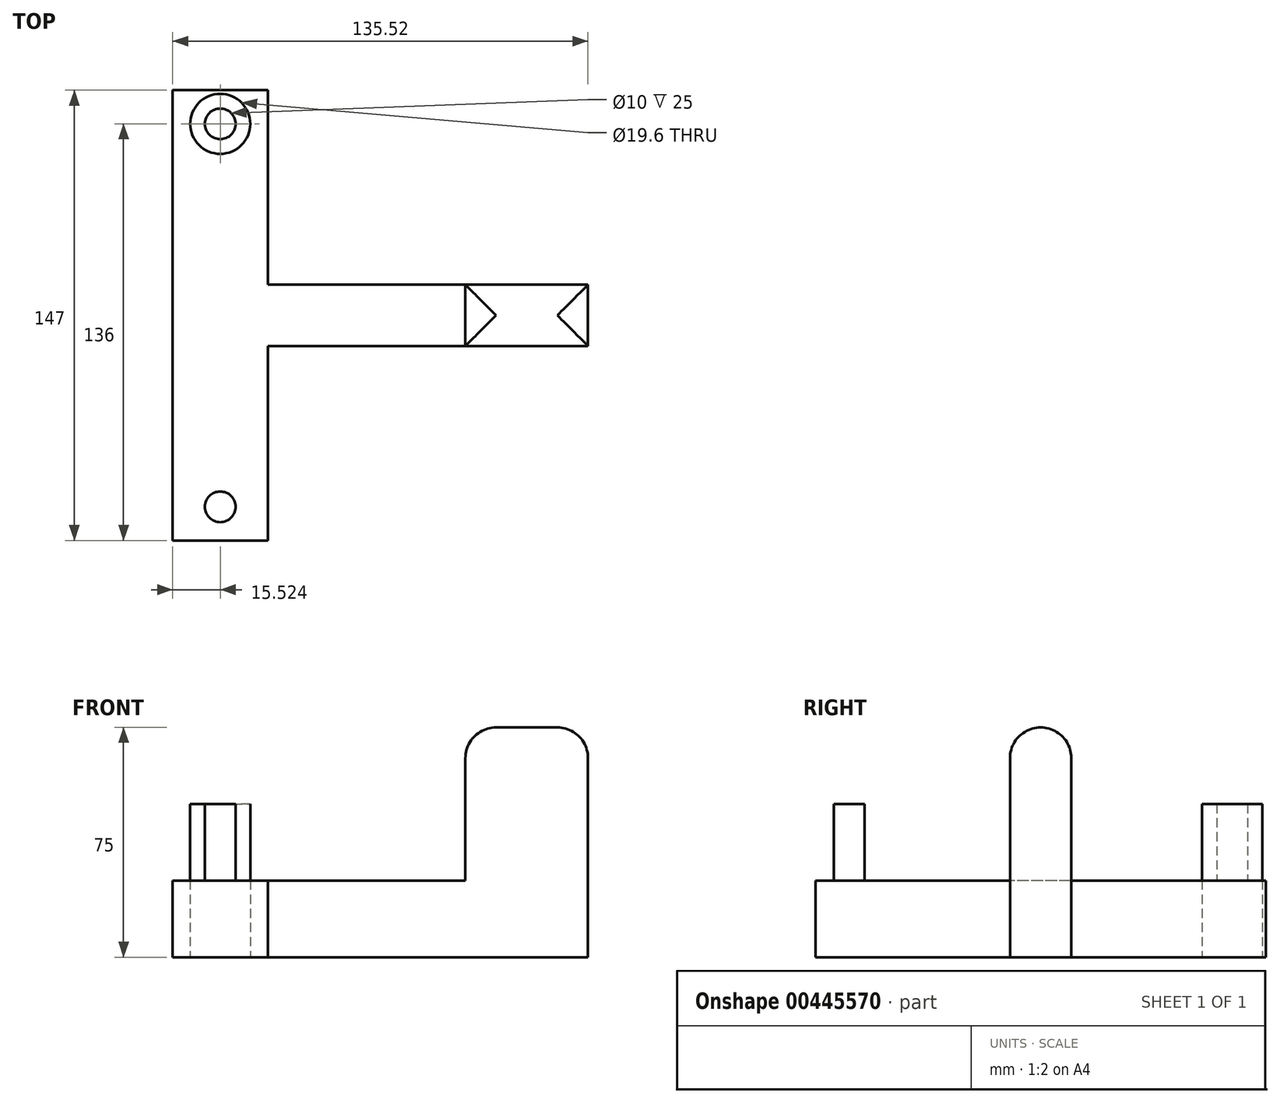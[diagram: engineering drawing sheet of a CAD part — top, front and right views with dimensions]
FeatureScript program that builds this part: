
annotation { "Feature Type Name" : "Feature", "Feature Type Description" : "" }
export const myFeature = defineFeature(function(context is Context, id is Id, definition is map)
    precondition{}
    {
        {
            var Q0;
            Q0=qCreatedBy(makeId("Top.planeOp"),FACE);
            var sketch = newSketch(context, id + "F0", { "sketchPlane" : qUnion([Q0])});
            skLineSegment(sketch, "E0.bottom", {"start": v(67.76, -10) * mm, "end": v(-67.76, -10) * mm});
            skLineSegment(sketch, "E0.top", {"start": v(67.76, 10) * mm, "end": v(-67.76, 10) * mm});
            skLineSegment(sketch, "E0.left", {"start": v(67.76, -10) * mm, "end": v(67.76, 10) * mm});
            skLineSegment(sketch, "E0.right", {"start": v(-67.76, -10) * mm, "end": v(-67.76, 10) * mm});
            skPoint(sketch, "E0.middle", {"position": v(0, 0) * mm});
            skLineSegment(sketch, "E1.bottom", {"start": v(27.76, 5.5) * mm, "end": v(67.76, 5.5) * mm});
            skLineSegment(sketch, "E1.top", {"start": v(27.76, 0) * mm, "end": v(67.76, 0) * mm});
            skLineSegment(sketch, "E1.left", {"start": v(27.76, 5.5) * mm, "end": v(27.76, 0) * mm});
            skLineSegment(sketch, "E1.right", {"start": v(67.76, 5.5) * mm, "end": v(67.76, 0) * mm});
            skLineSegment(sketch, "E2.MirrorCS", {"start": v(27.76, -5.5) * mm, "end": v(27.76, 0) * mm});
            skLineSegment(sketch, "E3.MirrorCS", {"start": v(27.76, -5.5) * mm, "end": v(67.76, -5.5) * mm});
            skCircle(sketch, "E4", {"center": v(-52.24, 62.5) * mm, "radius": 5 * mm});
            skCircle(sketch, "E5.MirrorC", {"center": v(-52.24, -62.5) * mm, "radius": 5 * mm});
            skLineSegment(sketch, "E6.bottom", {"start": v(-36.63, 73.5) * mm, "end": v(-67.76, 73.5) * mm});
            skLineSegment(sketch, "E6.top", {"start": v(-36.63, 10) * mm, "end": v(-67.76, 10) * mm});
            skLineSegment(sketch, "E6.left", {"start": v(-36.63, 73.5) * mm, "end": v(-36.63, 10) * mm});
            skLineSegment(sketch, "E6.right", {"start": v(-67.76, 73.5) * mm, "end": v(-67.76, 10) * mm});
            skLineSegment(sketch, "E7.MirrorCS", {"start": v(-67.76, -73.5) * mm, "end": v(-67.76, -10) * mm});
            skLineSegment(sketch, "E8.MirrorCS", {"start": v(-36.63, -73.5) * mm, "end": v(-36.63, -10) * mm});
            skLineSegment(sketch, "E9.MirrorCS", {"start": v(-36.63, -73.5) * mm, "end": v(-67.76, -73.5) * mm});
            skLineSegment(sketch, "E10", {"start": v(27.76, -5.5) * mm, "end": v(27.76, -10) * mm});
            skLineSegment(sketch, "E11", {"start": v(27.76, -10) * mm, "end": v(27.76, 5.5) * mm});
            skLineSegment(sketch, "E12", {"start": v(27.76, 5.5) * mm, "end": v(27.76, 10) * mm});
            skCircle(sketch, "E13", {"center": v(-52.24, 62.5) * mm, "radius": 9.8 * mm});
            skCircle(sketch, "E14.MirrorC", {"center": v(-52.24, -62.5) * mm, "radius": 9.8 * mm});
            skSolve(sketch);
        }
        {
            var Q0;
            Q0=makeQuery(id+"F0.imprint","IMPRINT",FACE,{"disambiguationData":[TD([[makeQuery(id+"F0.imprint","IMPRINT",EDGE,{"derivedFrom":sQuery(id+"F0.wireOp",EDGE,"E5.MirrorC")}),1.0]])]});
            var Q1;
            Q1=makeQuery(id+"F0.imprint","IMPRINT",FACE,{"disambiguationData":[TD([[makeQuery(id+"F0.imprint","IMPRINT",EDGE,{"derivedFrom":sQuery(id+"F0.wireOp",EDGE,"E4")}),-1.0]])]});
            extrude(context, id + "F1", {"entities" : qUnion([Q0, Q1]), "depth" : 50 * mm});
        }
        {
            var Q0;
            Q0=makeQuery(id+"F0.imprint","IMPRINT",FACE,{"disambiguationData":[TD([[makeQuery(id+"F0.imprint","IMPRINT",EDGE,{"derivedFrom":sQuery(id+"F0.wireOp",EDGE,"E6.bottom")}),1.0]])]});
            var Q1;
            {var subQ0=sQuery(id+"F0.wireOp",EDGE,"E0.right");Q1=makeQuery(id+"F0.imprint","IMPRINT",FACE,{"disambiguationData":[TD([[makeQuery(id+"F0.imprint","IMPRINT",EDGE,{"derivedFrom":subQ0}),-1.0]])]});}
            var Q2;
            {var subQ1=sQuery(id+"F0.wireOp",EDGE,"E7.MirrorCS");Q2=makeQuery(id+"F0.imprint","IMPRINT",FACE,{"disambiguationData":[TD([[makeQuery(id+"F0.imprint","IMPRINT",EDGE,{"derivedFrom":subQ1}),-1.0]])]});}
            extrude(context, id + "F2", {"entities" : qUnion([Q0, Q1, Q2]), "depth" : 25 * mm});
        }
        {
            var Q0;
            {var subQ5=sQuery(id+"F0.wireOp",EDGE,"E3.MirrorCS");Q0=makeQuery(id+"F0.imprint","IMPRINT",FACE,{"disambiguationData":[TD([[makeQuery(id+"F0.imprint","IMPRINT",EDGE,{"derivedFrom":subQ5}),-1.0]])]});}
            var Q1;
            {var subQ0=sQuery(id+"F0.wireOp",EDGE,"E1.top");Q1=makeQuery(id+"F0.imprint","IMPRINT",FACE,{"disambiguationData":[TD([[makeQuery(id+"F0.imprint","IMPRINT",EDGE,{"derivedFrom":subQ0}),-1.0]])]});}
            var Q2;
            {var subQ0=sQuery(id+"F0.wireOp",EDGE,"E1.bottom");Q2=makeQuery(id+"F0.imprint","IMPRINT",FACE,{"disambiguationData":[TD([[makeQuery(id+"F0.imprint","IMPRINT",EDGE,{"derivedFrom":subQ0}),-1.0]])]});}
            var Q3;
            {var subQ4=sQuery(id+"F0.wireOp",EDGE,"E1.bottom");Q3=makeQuery(id+"F0.imprint","IMPRINT",FACE,{"disambiguationData":[TD([[makeQuery(id+"F0.imprint","IMPRINT",EDGE,{"derivedFrom":subQ4}),1.0]])]});}
            extrude(context, id + "F3", {"entities" : qUnion([Q0, Q1, Q2, Q3]), "operationType" : NewBodyOperationType.ADD, "depth" : 75 * mm});
        }
        {
            var Q0;
            Q0=makeQuery(id+"F3.opExtrude","CAP_FACE",FACE,{"disambiguationData":[OSD([sQuery(id+"F0.wireOp",EDGE,"E0.bottom"),sQuery(id+"F0.wireOp",EDGE,"E0.top"),sQuery(id+"F0.wireOp",EDGE,"E0.left"),sQuery(id+"F0.wireOp",EDGE,"E1.right"),sQuery(id+"F0.wireOp",EDGE,"E11"),sQuery(id+"F0.wireOp",EDGE,"E12")])],"isStart":false});
            fillet(context, id + "F4", {"entities" : qUnion([Q0]), "radius" : 10 * mm, "allowEdgeOverflow" : false});
        }
        {
            var Q0;
            Q0=makeQuery(id+"F0.imprint","IMPRINT",FACE,{"disambiguationData":[TD([[makeQuery(id+"F0.imprint","IMPRINT",EDGE,{"derivedFrom":sQuery(id+"F0.wireOp",EDGE,"E4")}),1.0]])]});
            var Q1;
            Q1=makeQuery(id+"F0.imprint","IMPRINT",FACE,{"disambiguationData":[TD([[makeQuery(id+"F0.imprint","IMPRINT",EDGE,{"derivedFrom":sQuery(id+"F0.wireOp",EDGE,"E5.MirrorC")}),-1.0]])]});
            extrude(context, id + "F5", {"entities" : qUnion([Q0, Q1]), "operationType" : NewBodyOperationType.ADD, "depth" : 25 * mm});
        }
    });
